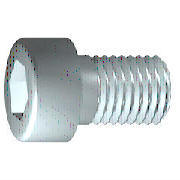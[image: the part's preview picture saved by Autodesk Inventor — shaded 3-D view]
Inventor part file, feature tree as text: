
AUTODESK INVENTOR PART (.ipt)
format: ipt  version: 2022 (Build 260153000, 153)  size: 198,144 bytes
history: native  units: mm (DEFAULTED — no unit token found)
features: sketch x2, other x1, extrude x1, plane x1, fillet x1
ambient origin geometry x7: Origin, YZ Plane, XY Plane, X Axis, Y Axis, Z Axis, Center Point
bodies: Solid1 (feature_tree)
feature tree (6):
  other  "Базовый элемент"
  extrude  "Паз"  Depth=7.6mm
  plane  "Work Plane1"
  fillet  "Fillet2"  Radius=0.49086mm
  sketch  "Эскиз1"
  sketch  "Эскиз2"
